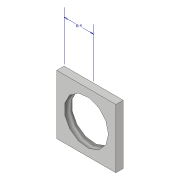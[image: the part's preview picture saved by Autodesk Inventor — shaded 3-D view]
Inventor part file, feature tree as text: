
AUTODESK INVENTOR PART (.ipt)
format: ipt  version: 2019 (Build 230136000, 136)  size: 92,160 bytes
history: native  units: in
note: dims shown in document units (in); Inventor stores cm internally (conversion verified against a paired STEP export)
features: sketch x3, extrude x2, thread x1
ambient origin geometry x8: Origin, YZ Plane, XZ Plane, XY Plane, X Axis, Y Axis, Z Axis, Center Point
bodies: Solid1 (feature_tree)
feature tree (6):
  sketch  "Sketch1"  dims[d0=0.315in d1=0.315in]
  sketch  "Sketch2"  dims[d2=0.1575in d3=0.0394in d4=0.0in d5=0.1575in]
  extrude  "Extrusion1"  Depth=0.315in
  extrude  "Extrusion2"  Depth=0.0394in TaperAngle=0.0deg
  thread  "Thread1"  [1 undecoded]
  sketch  "Sketch3"  dims[d6=0.1575in d7=0.2362in d8=0.1969in d9=0.0in d10=0.3937in d11=0.0in]
note: 1 required parameter value undecoded (feature->parameter linkage not recoverable at this tier; creation-order binding heuristic only, values carry confidence <= 0.55)
